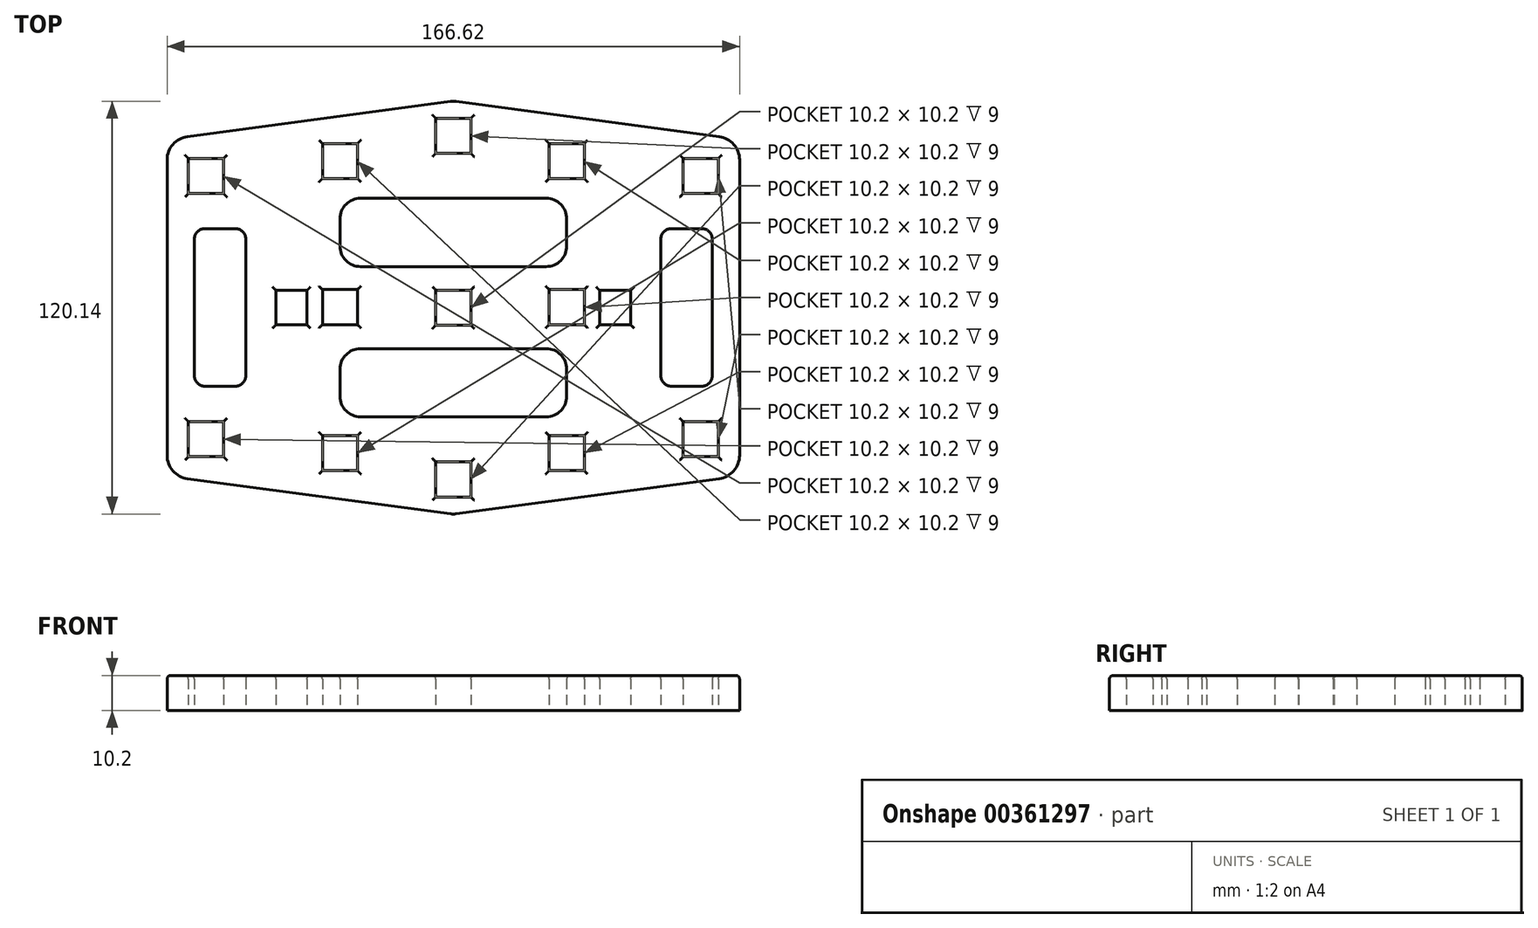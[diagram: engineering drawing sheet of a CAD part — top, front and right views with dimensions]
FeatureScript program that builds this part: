
annotation { "Feature Type Name" : "Feature", "Feature Type Description" : "" }
export const myFeature = defineFeature(function(context is Context, id is Id, definition is map)
    precondition{}
    {
        {
            var Q0;
            Q0=qCreatedBy(makeId("Top.planeOp"),FACE);
            var sketch = newSketch(context, id + "F0", { "sketchPlane" : qUnion([Q0])});
            skLineSegment(sketch, "E0.bottom", {"start": v(5.1, -5.1) * mm, "end": v(-5.1, -5.1) * mm});
            skLineSegment(sketch, "E0.top", {"start": v(5.1, 5.1) * mm, "end": v(-5.1, 5.1) * mm});
            skLineSegment(sketch, "E0.left", {"start": v(5.1, -5.1) * mm, "end": v(5.1, 5.1) * mm});
            skLineSegment(sketch, "E0.right", {"start": v(-5.1, -5.1) * mm, "end": v(-5.1, 5.1) * mm});
            skPoint(sketch, "E0.middle", {"position": v(0, 0) * mm});
            skCircle(sketch, "E1", {"center": v(0, 0) * mm, "radius": 50 * mm, "construction": true});
            skLineSegment(sketch, "E2.bottom", {"start": v(5.1, 44.9) * mm, "end": v(-5.1, 44.9) * mm});
            skLineSegment(sketch, "E2.top", {"start": v(5.1, 55.1) * mm, "end": v(-5.1, 55.1) * mm});
            skLineSegment(sketch, "E2.left", {"start": v(5.1, 44.9) * mm, "end": v(5.1, 55.1) * mm});
            skLineSegment(sketch, "E2.right", {"start": v(-5.1, 44.9) * mm, "end": v(-5.1, 55.1) * mm});
            skPoint(sketch, "E2.middle", {"position": v(0, 50) * mm});
            skLineSegment(sketch, "E3.bottom", {"start": v(5.1, -55.1) * mm, "end": v(-5.1, -55.1) * mm});
            skLineSegment(sketch, "E3.top", {"start": v(5.1, -44.9) * mm, "end": v(-5.1, -44.9) * mm});
            skLineSegment(sketch, "E3.left", {"start": v(5.1, -55.1) * mm, "end": v(5.1, -44.9) * mm});
            skLineSegment(sketch, "E3.right", {"start": v(-5.1, -55.1) * mm, "end": v(-5.1, -44.9) * mm});
            skPoint(sketch, "E3.middle", {"position": v(0, -50) * mm});
            skCircle(sketch, "E4", {"center": v(0, 0) * mm, "radius": 33 * mm, "construction": true});
            skLineSegment(sketch, "E5", {"start": v(-33, 25.81) * mm, "end": v(-33, 17.94) * mm});
            skCircle(sketch, "E6", {"center": v(-33, 0.15) * mm, "radius": 42.5 * mm, "construction": true});
            skPoint(sketch, "E7.middle", {"position": v(-33, 42.65) * mm});
            skLineSegment(sketch, "E8.bottom", {"start": v(-27.9, 5.25) * mm, "end": v(-38.1, 5.25) * mm});
            skLineSegment(sketch, "E8.top", {"start": v(-27.9, -4.95) * mm, "end": v(-38.1, -4.95) * mm});
            skLineSegment(sketch, "E8.left", {"start": v(-27.9, 5.25) * mm, "end": v(-27.9, -4.95) * mm});
            skLineSegment(sketch, "E8.right", {"start": v(-38.1, 5.25) * mm, "end": v(-38.1, -4.95) * mm});
            skLineSegment(sketch, "E9.bottom", {"start": v(-38.1, 37.55) * mm, "end": v(-27.9, 37.55) * mm});
            skLineSegment(sketch, "E9.top", {"start": v(-38.1, 47.75) * mm, "end": v(-27.9, 47.75) * mm});
            skLineSegment(sketch, "E9.left", {"start": v(-38.1, 37.55) * mm, "end": v(-38.1, 47.75) * mm});
            skLineSegment(sketch, "E9.right", {"start": v(-27.9, 37.55) * mm, "end": v(-27.9, 47.75) * mm});
            skLineSegment(sketch, "E10.bottom", {"start": v(-27.9, -47.45) * mm, "end": v(-38.1, -47.45) * mm});
            skLineSegment(sketch, "E10.top", {"start": v(-27.9, -37.25) * mm, "end": v(-38.1, -37.25) * mm});
            skLineSegment(sketch, "E10.left", {"start": v(-27.9, -47.45) * mm, "end": v(-27.9, -37.25) * mm});
            skLineSegment(sketch, "E10.right", {"start": v(-38.1, -47.45) * mm, "end": v(-38.1, -37.25) * mm});
            skPoint(sketch, "E10.middle", {"position": v(-33, -42.35) * mm});
            skCircle(sketch, "E11", {"center": v(-33, 0.15) * mm, "radius": 39 * mm, "construction": true});
            skLineSegment(sketch, "E12", {"start": v(-72, 50.1) * mm, "end": v(-72, -61.27) * mm, "construction": true});
            skCircle(sketch, "E13", {"center": v(-72, 0) * mm, "radius": 38.3 * mm, "construction": true});
            skLineSegment(sketch, "E14.bottom", {"start": v(-77.1, 33.2) * mm, "end": v(-66.9, 33.2) * mm});
            skLineSegment(sketch, "E14.top", {"start": v(-77.1, 43.4) * mm, "end": v(-66.9, 43.4) * mm});
            skLineSegment(sketch, "E14.left", {"start": v(-77.1, 33.2) * mm, "end": v(-77.1, 43.4) * mm});
            skLineSegment(sketch, "E14.right", {"start": v(-66.9, 33.2) * mm, "end": v(-66.9, 43.4) * mm});
            skPoint(sketch, "E14.middle", {"position": v(-72, 38.3) * mm});
            skLineSegment(sketch, "E15.bottom", {"start": v(-77.1, -43.4) * mm, "end": v(-66.9, -43.4) * mm});
            skLineSegment(sketch, "E15.top", {"start": v(-77.1, -33.2) * mm, "end": v(-66.9, -33.2) * mm});
            skLineSegment(sketch, "E15.left", {"start": v(-77.1, -43.4) * mm, "end": v(-77.1, -33.2) * mm});
            skLineSegment(sketch, "E15.right", {"start": v(-66.9, -43.4) * mm, "end": v(-66.9, -33.2) * mm});
            skPoint(sketch, "E15.middle", {"position": v(-72, -38.3) * mm});
            skLineSegment(sketch, "E16.MirrorCS", {"start": v(27.9, -4.95) * mm, "end": v(38.1, -4.95) * mm});
            skPoint(sketch, "E17.MirrorP", {"position": v(33, 42.65) * mm});
            skLineSegment(sketch, "E18.MirrorCS", {"start": v(66.9, 33.2) * mm, "end": v(66.9, 43.4) * mm});
            skLineSegment(sketch, "E19.MirrorCS", {"start": v(27.9, 5.25) * mm, "end": v(27.9, -4.95) * mm});
            skLineSegment(sketch, "E20.MirrorCS", {"start": v(66.9, -43.4) * mm, "end": v(66.9, -33.2) * mm});
            skLineSegment(sketch, "E21.MirrorCS", {"start": v(77.1, 33.2) * mm, "end": v(66.9, 33.2) * mm});
            skLineSegment(sketch, "E22.MirrorCS", {"start": v(38.1, 37.55) * mm, "end": v(38.1, 47.75) * mm});
            skLineSegment(sketch, "E23.MirrorCS", {"start": v(27.9, -37.25) * mm, "end": v(38.1, -37.25) * mm});
            skLineSegment(sketch, "E24.MirrorCS", {"start": v(77.1, 33.2) * mm, "end": v(77.1, 43.4) * mm});
            skLineSegment(sketch, "E25.MirrorCS", {"start": v(77.1, -43.4) * mm, "end": v(77.1, -33.2) * mm});
            skLineSegment(sketch, "E26.MirrorCS", {"start": v(38.1, 5.25) * mm, "end": v(38.1, -4.95) * mm});
            skPoint(sketch, "E27.MirrorP", {"position": v(33, 0.15) * mm});
            skLineSegment(sketch, "E28.MirrorCS", {"start": v(38.1, 37.55) * mm, "end": v(27.9, 37.55) * mm});
            skLineSegment(sketch, "E29.MirrorCS", {"start": v(27.9, 37.55) * mm, "end": v(27.9, 47.75) * mm});
            skPoint(sketch, "E30.MirrorP", {"position": v(72, 38.3) * mm});
            skLineSegment(sketch, "E31.MirrorCS", {"start": v(38.1, -47.45) * mm, "end": v(38.1, -37.25) * mm});
            skLineSegment(sketch, "E32.MirrorCS", {"start": v(38.1, 47.75) * mm, "end": v(27.9, 47.75) * mm});
            skLineSegment(sketch, "E33.MirrorCS", {"start": v(77.1, -33.2) * mm, "end": v(66.9, -33.2) * mm});
            skLineSegment(sketch, "E34.MirrorCS", {"start": v(33, 25.81) * mm, "end": v(33, 17.94) * mm});
            skLineSegment(sketch, "E35.MirrorCS", {"start": v(72, 50.1) * mm, "end": v(72, -61.27) * mm, "construction": true});
            skLineSegment(sketch, "E36.MirrorCS", {"start": v(27.9, 5.25) * mm, "end": v(38.1, 5.25) * mm});
            skLineSegment(sketch, "E37.MirrorCS", {"start": v(77.1, -43.4) * mm, "end": v(66.9, -43.4) * mm});
            skLineSegment(sketch, "E38.MirrorCS", {"start": v(77.1, 43.4) * mm, "end": v(66.9, 43.4) * mm});
            skPoint(sketch, "E39.MirrorP", {"position": v(72, -38.3) * mm});
            skLineSegment(sketch, "E40.MirrorCS", {"start": v(27.9, -47.45) * mm, "end": v(27.9, -37.25) * mm});
            skLineSegment(sketch, "E41.MirrorCS", {"start": v(27.9, -47.45) * mm, "end": v(38.1, -47.45) * mm});
            skPoint(sketch, "E42.MirrorP", {"position": v(33, -42.35) * mm});
            skLineSegment(sketch, "E43", {"start": v(-0.8, 60.02) * mm, "end": v(-52.3, 53.14) * mm});
            skLineSegment(sketch, "E44", {"start": v(-83.3, 43) * mm, "end": v(-83.3, 0) * mm});
            skPoint(sketch, "E45.visualSharp", {"position": v(-83.3, 49) * mm});
            skLineSegment(sketch, "E46.MirrorCS", {"start": v(-0.8, -60.02) * mm, "end": v(-52.3, -53.14) * mm});
            skLineSegment(sketch, "E47.MirrorCS", {"start": v(-83.3, -43) * mm, "end": v(-83.3, 0) * mm});
            skLineSegment(sketch, "E48.MirrorCS", {"start": v(0.8, -60.02) * mm, "end": v(52.3, -53.14) * mm});
            skLineSegment(sketch, "E49.MirrorCS", {"start": v(83.3, -43) * mm, "end": v(83.3, 0) * mm});
            skLineSegment(sketch, "E50.MirrorCS", {"start": v(0.8, 60.02) * mm, "end": v(52.3, 53.14) * mm});
            skLineSegment(sketch, "E51.MirrorCS", {"start": v(83.3, 43) * mm, "end": v(83.3, 0) * mm});
            skPoint(sketch, "E52.visualSharp", {"position": v(0, 60.12) * mm});
            skArc(sketch, "E52.filletArc", {"start": v(0.8, 60.02) * mm, "mid": v(0, 60.07) * mm, "end": v(-0.8, 60.02) * mm});
            skPoint(sketch, "E53.visualSharp", {"position": v(0, -60.12) * mm});
            skArc(sketch, "E53.filletArc", {"start": v(-0.8, -60.02) * mm, "mid": v(0, -60.07) * mm, "end": v(0.8, -60.02) * mm});
            skPoint(sketch, "E54.visualSharp", {"position": v(-75.36, 23) * mm});
            skPoint(sketch, "E55.visualSharp", {"position": v(-44.4, 23) * mm});
            skPoint(sketch, "E56.visualSharp", {"position": v(-44.4, -22.92) * mm});
            skPoint(sketch, "E57.visualSharp", {"position": v(-75.36, -22.92) * mm});
            skLineSegment(sketch, "E58.bottom", {"start": v(-27, 31.81) * mm, "end": v(27, 31.81) * mm});
            skLineSegment(sketch, "E58.top", {"start": v(-27, 11.94) * mm, "end": v(27, 11.94) * mm});
            skPoint(sketch, "E59.newPointB", {"position": v(-33, 73.57) * mm});
            skArc(sketch, "E59.filletArc", {"start": v(-27, 31.81) * mm, "mid": v(-31.24, 30.05) * mm, "end": v(-33, 25.81) * mm});
            skPoint(sketch, "E60.newPointA", {"position": v(-33, -73.26) * mm});
            skArc(sketch, "E60.filletArc", {"start": v(-33, 17.94) * mm, "mid": v(-31.24, 13.7) * mm, "end": v(-27, 11.94) * mm});
            skPoint(sketch, "E61.newPointB", {"position": v(33, -73.26) * mm});
            skArc(sketch, "E61.filletArc", {"start": v(27, 11.94) * mm, "mid": v(31.24, 13.7) * mm, "end": v(33, 17.94) * mm});
            skPoint(sketch, "E62.newPointB", {"position": v(33, 73.57) * mm});
            skArc(sketch, "E62.filletArc", {"start": v(33, 25.81) * mm, "mid": v(31.24, 30.05) * mm, "end": v(27, 31.81) * mm});
            skLineSegment(sketch, "E63.MirrorCS", {"start": v(-27, -31.81) * mm, "end": v(27, -31.81) * mm});
            skArc(sketch, "E64.MirrorCS", {"start": v(33, -25.81) * mm, "mid": v(31.24, -30.05) * mm, "end": v(27, -31.81) * mm});
            skLineSegment(sketch, "E65.MirrorCS", {"start": v(-33, -25.81) * mm, "end": v(-33, -17.94) * mm});
            skLineSegment(sketch, "E66.MirrorCS", {"start": v(33, -25.81) * mm, "end": v(33, -17.94) * mm});
            skArc(sketch, "E67.MirrorCS", {"start": v(27, -11.94) * mm, "mid": v(31.24, -13.7) * mm, "end": v(33, -17.94) * mm});
            skLineSegment(sketch, "E68.MirrorCS", {"start": v(-27, -11.94) * mm, "end": v(27, -11.94) * mm});
            skArc(sketch, "E69.MirrorCS", {"start": v(-33, -17.94) * mm, "mid": v(-31.24, -13.7) * mm, "end": v(-27, -11.94) * mm});
            skArc(sketch, "E70.MirrorCS", {"start": v(-27, -31.81) * mm, "mid": v(-31.24, -30.05) * mm, "end": v(-33, -25.81) * mm});
            skCircle(sketch, "E71", {"center": v(-42.1, 0) * mm, "radius": 5 * mm, "construction": true});
            skLineSegment(sketch, "E72.bottom", {"start": v(-51.6, -5) * mm, "end": v(-42.6, -5) * mm});
            skLineSegment(sketch, "E72.top", {"start": v(-51.6, 5) * mm, "end": v(-42.6, 5) * mm});
            skLineSegment(sketch, "E72.left", {"start": v(-51.6, -5) * mm, "end": v(-51.6, 5) * mm});
            skLineSegment(sketch, "E72.right", {"start": v(-42.6, -5) * mm, "end": v(-42.6, 5) * mm});
            skPoint(sketch, "E72.middle", {"position": v(-47.1, 0) * mm});
            skLineSegment(sketch, "E73.MirrorCS", {"start": v(51.6, -5) * mm, "end": v(51.6, 5) * mm});
            skLineSegment(sketch, "E74.MirrorCS", {"start": v(51.6, -5) * mm, "end": v(42.6, -5) * mm});
            skLineSegment(sketch, "E75.MirrorCS", {"start": v(51.6, 5) * mm, "end": v(42.6, 5) * mm});
            skLineSegment(sketch, "E76.MirrorCS", {"start": v(42.6, -5) * mm, "end": v(42.6, 5) * mm});
            skLineSegment(sketch, "E77.bottom", {"start": v(-72.36, 23) * mm, "end": v(-63.43, 23) * mm});
            skLineSegment(sketch, "E77.top", {"start": v(-72.36, -22.88) * mm, "end": v(-63.43, -22.88) * mm});
            skLineSegment(sketch, "E77.left", {"start": v(-75.36, 20) * mm, "end": v(-75.36, -19.88) * mm});
            skLineSegment(sketch, "E77.right", {"start": v(-60.43, 20) * mm, "end": v(-60.43, -19.88) * mm});
            skArc(sketch, "E78.filletArc", {"start": v(-72.36, 23) * mm, "mid": v(-74.48, 22.12) * mm, "end": v(-75.36, 20) * mm});
            skPoint(sketch, "E79.visualSharp", {"position": v(-75.36, -22.88) * mm});
            skArc(sketch, "E79.filletArc", {"start": v(-75.36, -19.88) * mm, "mid": v(-74.48, -22) * mm, "end": v(-72.36, -22.88) * mm});
            skPoint(sketch, "E80.visualSharp", {"position": v(-60.43, 23) * mm});
            skArc(sketch, "E80.filletArc", {"start": v(-60.43, 20) * mm, "mid": v(-61.3, 22.12) * mm, "end": v(-63.43, 23) * mm});
            skPoint(sketch, "E81.visualSharp", {"position": v(-60.43, -22.88) * mm});
            skArc(sketch, "E81.filletArc", {"start": v(-63.43, -22.88) * mm, "mid": v(-61.3, -22) * mm, "end": v(-60.43, -19.88) * mm});
            skArc(sketch, "E82.MirrorCS", {"start": v(60.43, 20) * mm, "mid": v(61.3, 22.12) * mm, "end": v(63.43, 23) * mm});
            skLineSegment(sketch, "E83.MirrorCS", {"start": v(60.43, 20) * mm, "end": v(60.43, -19.88) * mm});
            skArc(sketch, "E84.MirrorCS", {"start": v(63.43, -22.88) * mm, "mid": v(61.3, -22) * mm, "end": v(60.43, -19.88) * mm});
            skLineSegment(sketch, "E85.MirrorCS", {"start": v(72.36, -22.88) * mm, "end": v(63.43, -22.88) * mm});
            skArc(sketch, "E86.MirrorCS", {"start": v(75.36, -19.88) * mm, "mid": v(74.48, -22) * mm, "end": v(72.36, -22.88) * mm});
            skLineSegment(sketch, "E87.MirrorCS", {"start": v(72.36, 23) * mm, "end": v(63.43, 23) * mm});
            skLineSegment(sketch, "E88.MirrorCS", {"start": v(75.36, 20) * mm, "end": v(75.36, -19.88) * mm});
            skArc(sketch, "E89.MirrorCS", {"start": v(72.36, 23) * mm, "mid": v(74.48, 22.12) * mm, "end": v(75.36, 20) * mm});
            skLineSegment(sketch, "E90.trimOffspring", {"start": v(-62.22, 51.81) * mm, "end": v(-77.36, 49.8) * mm});
            skLineSegment(sketch, "E91.trimOffspring", {"start": v(62.22, 51.81) * mm, "end": v(77.36, 49.8) * mm});
            skLineSegment(sketch, "E92.trimOffspring", {"start": v(-62.22, -51.81) * mm, "end": v(-77.36, -49.8) * mm});
            skLineSegment(sketch, "E93.trimOffspring", {"start": v(62.22, -51.81) * mm, "end": v(77.36, -49.8) * mm});
            skLineSegment(sketch, "E94", {"start": v(-62.22, 51.81) * mm, "end": v(-52.3, 53.14) * mm});
            skLineSegment(sketch, "E95", {"start": v(52.3, 53.14) * mm, "end": v(62.22, 51.81) * mm});
            skLineSegment(sketch, "E96", {"start": v(62.22, -51.81) * mm, "end": v(52.3, -53.14) * mm});
            skLineSegment(sketch, "E97", {"start": v(-52.3, -53.14) * mm, "end": v(-62.22, -51.81) * mm});
            skPoint(sketch, "E98.orphan", {"position": v(-83.3, 43.74) * mm});
            skPoint(sketch, "E99.orphan", {"position": v(83.3, 43.74) * mm});
            skPoint(sketch, "E100.orphan", {"position": v(83.3, -43.74) * mm});
            skPoint(sketch, "E101.orphan", {"position": v(-83.3, -43.74) * mm});
            skPoint(sketch, "E102.newPointA", {"position": v(-78.1, 49.7) * mm});
            skArc(sketch, "E102.filletArc", {"start": v(-77.36, 49.8) * mm, "mid": v(-81.61, 47.51) * mm, "end": v(-83.3, 43) * mm});
            skArc(sketch, "E103.MirrorCS", {"start": v(77.36, 49.8) * mm, "mid": v(81.61, 47.51) * mm, "end": v(83.3, 43) * mm});
            skPoint(sketch, "E104.orphan", {"position": v(78.1, 49.7) * mm});
            skArc(sketch, "E105.MirrorCS", {"start": v(-77.36, -49.8) * mm, "mid": v(-81.61, -47.51) * mm, "end": v(-83.3, -43) * mm});
            skPoint(sketch, "E106.orphan", {"position": v(-78.1, -49.7) * mm});
            skArc(sketch, "E107.MirrorCS", {"start": v(77.36, -49.8) * mm, "mid": v(81.61, -47.51) * mm, "end": v(83.3, -43) * mm});
            skPoint(sketch, "E108.orphan", {"position": v(78.1, -49.7) * mm});
            skSolve(sketch);
        }
        {
            var Q0;
            Q0=makeQuery(id+"F0.imprint","IMPRINT",FACE,{"disambiguationData":[TD([[makeQuery(id+"F0.imprint","IMPRINT",EDGE,{"derivedFrom":sQuery(id+"F0.wireOp",EDGE,"E0.bottom")}),1.0]])]});
            extrude(context, id + "F1", {"entities" : qUnion([Q0]), "depth" : 10 * mm});
        }
        {
            var Q0;
            Q0=makeQuery(id+"F1.opExtrude","CAP_FACE",FACE,{"disambiguationData":[OSD([sQuery(id+"F0.wireOp",EDGE,"E0.bottom"),sQuery(id+"F0.wireOp",EDGE,"E0.top"),sQuery(id+"F0.wireOp",EDGE,"E0.left"),sQuery(id+"F0.wireOp",EDGE,"E0.right"),sQuery(id+"F0.wireOp",EDGE,"E2.bottom"),sQuery(id+"F0.wireOp",EDGE,"E2.top"),sQuery(id+"F0.wireOp",EDGE,"E2.left"),sQuery(id+"F0.wireOp",EDGE,"E2.right"),sQuery(id+"F0.wireOp",EDGE,"E3.bottom"),sQuery(id+"F0.wireOp",EDGE,"E3.top"),sQuery(id+"F0.wireOp",EDGE,"E3.left"),sQuery(id+"F0.wireOp",EDGE,"E3.right"),sQuery(id+"F0.wireOp",EDGE,"E8.bottom"),sQuery(id+"F0.wireOp",EDGE,"E8.top"),sQuery(id+"F0.wireOp",EDGE,"E8.left"),sQuery(id+"F0.wireOp",EDGE,"E8.right"),sQuery(id+"F0.wireOp",EDGE,"E9.bottom"),sQuery(id+"F0.wireOp",EDGE,"E9.top"),sQuery(id+"F0.wireOp",EDGE,"E9.left"),sQuery(id+"F0.wireOp",EDGE,"E9.right"),sQuery(id+"F0.wireOp",EDGE,"E10.bottom"),sQuery(id+"F0.wireOp",EDGE,"E10.top"),sQuery(id+"F0.wireOp",EDGE,"E10.left"),sQuery(id+"F0.wireOp",EDGE,"E10.right"),sQuery(id+"F0.wireOp",EDGE,"E14.bottom"),sQuery(id+"F0.wireOp",EDGE,"E14.top"),sQuery(id+"F0.wireOp",EDGE,"E14.left"),sQuery(id+"F0.wireOp",EDGE,"E14.right"),sQuery(id+"F0.wireOp",EDGE,"E15.bottom"),sQuery(id+"F0.wireOp",EDGE,"E15.top"),sQuery(id+"F0.wireOp",EDGE,"E15.left"),sQuery(id+"F0.wireOp",EDGE,"E15.right"),sQuery(id+"F0.wireOp",EDGE,"E16.MirrorCS"),sQuery(id+"F0.wireOp",EDGE,"E18.MirrorCS"),sQuery(id+"F0.wireOp",EDGE,"E19.MirrorCS"),sQuery(id+"F0.wireOp",EDGE,"E20.MirrorCS"),sQuery(id+"F0.wireOp",EDGE,"E21.MirrorCS"),sQuery(id+"F0.wireOp",EDGE,"E22.MirrorCS"),sQuery(id+"F0.wireOp",EDGE,"E23.MirrorCS"),sQuery(id+"F0.wireOp",EDGE,"E24.MirrorCS"),sQuery(id+"F0.wireOp",EDGE,"E25.MirrorCS"),sQuery(id+"F0.wireOp",EDGE,"E26.MirrorCS"),sQuery(id+"F0.wireOp",EDGE,"E28.MirrorCS"),sQuery(id+"F0.wireOp",EDGE,"E29.MirrorCS"),sQuery(id+"F0.wireOp",EDGE,"E31.MirrorCS"),sQuery(id+"F0.wireOp",EDGE,"E32.MirrorCS"),sQuery(id+"F0.wireOp",EDGE,"E33.MirrorCS"),sQuery(id+"F0.wireOp",EDGE,"E36.MirrorCS"),sQuery(id+"F0.wireOp",EDGE,"E37.MirrorCS"),sQuery(id+"F0.wireOp",EDGE,"E38.MirrorCS"),sQuery(id+"F0.wireOp",EDGE,"E40.MirrorCS"),sQuery(id+"F0.wireOp",EDGE,"E41.MirrorCS"),sQuery(id+"F0.wireOp",EDGE,"E43"),sQuery(id+"F0.wireOp",EDGE,"E44"),sQuery(id+"F0.wireOp",EDGE,"E47.MirrorCS"),sQuery(id+"F0.wireOp",EDGE,"E46.MirrorCS"),sQuery(id+"F0.wireOp",EDGE,"E48.MirrorCS"),sQuery(id+"F0.wireOp",EDGE,"E49.MirrorCS"),sQuery(id+"F0.wireOp",EDGE,"E50.MirrorCS"),sQuery(id+"F0.wireOp",EDGE,"E51.MirrorCS"),sQuery(id+"F0.wireOp",EDGE,"E52.filletArc"),sQuery(id+"F0.wireOp",EDGE,"E53.filletArc"),sQuery(id+"F0.wireOp",EDGE,"E58.bottom"),sQuery(id+"F0.wireOp",EDGE,"E58.top"),sQuery(id+"F0.wireOp",EDGE,"E5"),sQuery(id+"F0.wireOp",EDGE,"E34.MirrorCS"),sQuery(id+"F0.wireOp",EDGE,"E59.filletArc"),sQuery(id+"F0.wireOp",EDGE,"E60.filletArc"),sQuery(id+"F0.wireOp",EDGE,"E61.filletArc"),sQuery(id+"F0.wireOp",EDGE,"E62.filletArc"),sQuery(id+"F0.wireOp",EDGE,"E63.MirrorCS"),sQuery(id+"F0.wireOp",EDGE,"E64.MirrorCS"),sQuery(id+"F0.wireOp",EDGE,"E65.MirrorCS"),sQuery(id+"F0.wireOp",EDGE,"E66.MirrorCS"),sQuery(id+"F0.wireOp",EDGE,"E67.MirrorCS"),sQuery(id+"F0.wireOp",EDGE,"E68.MirrorCS"),sQuery(id+"F0.wireOp",EDGE,"E69.MirrorCS"),sQuery(id+"F0.wireOp",EDGE,"E70.MirrorCS"),sQuery(id+"F0.wireOp",EDGE,"E72.bottom"),sQuery(id+"F0.wireOp",EDGE,"E72.top"),sQuery(id+"F0.wireOp",EDGE,"E72.left"),sQuery(id+"F0.wireOp",EDGE,"E72.right"),sQuery(id+"F0.wireOp",EDGE,"E73.MirrorCS"),sQuery(id+"F0.wireOp",EDGE,"E74.MirrorCS"),sQuery(id+"F0.wireOp",EDGE,"E75.MirrorCS"),sQuery(id+"F0.wireOp",EDGE,"E76.MirrorCS"),sQuery(id+"F0.wireOp",EDGE,"E77.bottom"),sQuery(id+"F0.wireOp",EDGE,"E77.top"),sQuery(id+"F0.wireOp",EDGE,"E77.left"),sQuery(id+"F0.wireOp",EDGE,"E77.right"),sQuery(id+"F0.wireOp",EDGE,"E78.filletArc"),sQuery(id+"F0.wireOp",EDGE,"E79.filletArc"),sQuery(id+"F0.wireOp",EDGE,"E80.filletArc"),sQuery(id+"F0.wireOp",EDGE,"E81.filletArc"),sQuery(id+"F0.wireOp",EDGE,"E82.MirrorCS"),sQuery(id+"F0.wireOp",EDGE,"E83.MirrorCS"),sQuery(id+"F0.wireOp",EDGE,"E84.MirrorCS"),sQuery(id+"F0.wireOp",EDGE,"E85.MirrorCS"),sQuery(id+"F0.wireOp",EDGE,"E86.MirrorCS"),sQuery(id+"F0.wireOp",EDGE,"E87.MirrorCS"),sQuery(id+"F0.wireOp",EDGE,"E88.MirrorCS"),sQuery(id+"F0.wireOp",EDGE,"E89.MirrorCS"),sQuery(id+"F0.wireOp",EDGE,"E90.trimOffspring"),sQuery(id+"F0.wireOp",EDGE,"E91.trimOffspring"),sQuery(id+"F0.wireOp",EDGE,"E92.trimOffspring"),sQuery(id+"F0.wireOp",EDGE,"E93.trimOffspring"),sQuery(id+"F0.wireOp",EDGE,"E94"),sQuery(id+"F0.wireOp",EDGE,"E95"),sQuery(id+"F0.wireOp",EDGE,"E96"),sQuery(id+"F0.wireOp",EDGE,"E97"),sQuery(id+"F0.wireOp",EDGE,"E102.filletArc"),sQuery(id+"F0.wireOp",EDGE,"E103.MirrorCS"),sQuery(id+"F0.wireOp",EDGE,"E105.MirrorCS"),sQuery(id+"F0.wireOp",EDGE,"E107.MirrorCS")])],"isStart":false});
            fillet(context, id + "F2", {"entities" : qUnion([Q0]), "radius" : 1 * mm, "tangentPropagation" : true, "allowEdgeOverflow" : false});
        }
        {
            var Q0;
            Q0=makeQuery(id+"F0.imprint","IMPRINT",FACE,{"disambiguationData":[TD([[makeQuery(id+"F0.imprint","IMPRINT",EDGE,{"derivedFrom":sQuery(id+"F0.wireOp",EDGE,"E9.bottom")}),1.0]])]});
            var Q1;
            Q1=makeQuery(id+"F0.imprint","IMPRINT",FACE,{"disambiguationData":[TD([[makeQuery(id+"F0.imprint","IMPRINT",EDGE,{"derivedFrom":sQuery(id+"F0.wireOp",EDGE,"E14.bottom")}),1.0]])]});
            var Q2;
            Q2=makeQuery(id+"F0.imprint","IMPRINT",FACE,{"disambiguationData":[TD([[makeQuery(id+"F0.imprint","IMPRINT",EDGE,{"derivedFrom":sQuery(id+"F0.wireOp",EDGE,"E77.bottom")}),-1.0]])]});
            var Q3;
            Q3=makeQuery(id+"F0.imprint","IMPRINT",FACE,{"disambiguationData":[TD([[makeQuery(id+"F0.imprint","IMPRINT",EDGE,{"derivedFrom":sQuery(id+"F0.wireOp",EDGE,"E58.bottom")}),-1.0]])]});
            var Q4;
            Q4=makeQuery(id+"F0.imprint","IMPRINT",FACE,{"disambiguationData":[TD([[makeQuery(id+"F0.imprint","IMPRINT",EDGE,{"derivedFrom":sQuery(id+"F0.wireOp",EDGE,"E2.bottom")}),-1.0]])]});
            var Q5;
            Q5=makeQuery(id+"F0.imprint","IMPRINT",FACE,{"disambiguationData":[TD([[makeQuery(id+"F0.imprint","IMPRINT",EDGE,{"derivedFrom":sQuery(id+"F0.wireOp",EDGE,"E22.MirrorCS")}),1.0]])]});
            var Q6;
            Q6=makeQuery(id+"F0.imprint","IMPRINT",FACE,{"disambiguationData":[TD([[makeQuery(id+"F0.imprint","IMPRINT",EDGE,{"derivedFrom":sQuery(id+"F0.wireOp",EDGE,"E18.MirrorCS")}),-1.0]])]});
            var Q7;
            Q7=makeQuery(id+"F0.imprint","IMPRINT",FACE,{"disambiguationData":[TD([[makeQuery(id+"F0.imprint","IMPRINT",EDGE,{"derivedFrom":sQuery(id+"F0.wireOp",EDGE,"E82.MirrorCS")}),-1.0]])]});
            var Q8;
            Q8=makeQuery(id+"F0.imprint","IMPRINT",FACE,{"disambiguationData":[TD([[makeQuery(id+"F0.imprint","IMPRINT",EDGE,{"derivedFrom":sQuery(id+"F0.wireOp",EDGE,"E73.MirrorCS")}),1.0]])]});
            var Q9;
            Q9=makeQuery(id+"F0.imprint","IMPRINT",FACE,{"disambiguationData":[TD([[makeQuery(id+"F0.imprint","IMPRINT",EDGE,{"derivedFrom":sQuery(id+"F0.wireOp",EDGE,"E16.MirrorCS")}),1.0]])]});
            var Q10;
            Q10=makeQuery(id+"F0.imprint","IMPRINT",FACE,{"disambiguationData":[TD([[makeQuery(id+"F0.imprint","IMPRINT",EDGE,{"derivedFrom":sQuery(id+"F0.wireOp",EDGE,"E0.bottom")}),-1.0]])]});
            var Q11;
            Q11=makeQuery(id+"F0.imprint","IMPRINT",FACE,{"disambiguationData":[TD([[makeQuery(id+"F0.imprint","IMPRINT",EDGE,{"derivedFrom":sQuery(id+"F0.wireOp",EDGE,"E63.MirrorCS")}),1.0]])]});
            var Q12;
            Q12=makeQuery(id+"F0.imprint","IMPRINT",FACE,{"disambiguationData":[TD([[makeQuery(id+"F0.imprint","IMPRINT",EDGE,{"derivedFrom":sQuery(id+"F0.wireOp",EDGE,"E8.bottom")}),1.0]])]});
            var Q13;
            Q13=makeQuery(id+"F0.imprint","IMPRINT",FACE,{"disambiguationData":[TD([[makeQuery(id+"F0.imprint","IMPRINT",EDGE,{"derivedFrom":sQuery(id+"F0.wireOp",EDGE,"E72.bottom")}),1.0]])]});
            var Q14;
            Q14=makeQuery(id+"F0.imprint","IMPRINT",FACE,{"disambiguationData":[TD([[makeQuery(id+"F0.imprint","IMPRINT",EDGE,{"derivedFrom":sQuery(id+"F0.wireOp",EDGE,"E15.bottom")}),1.0]])]});
            var Q15;
            Q15=makeQuery(id+"F0.imprint","IMPRINT",FACE,{"disambiguationData":[TD([[makeQuery(id+"F0.imprint","IMPRINT",EDGE,{"derivedFrom":sQuery(id+"F0.wireOp",EDGE,"E10.bottom")}),-1.0]])]});
            var Q16;
            Q16=makeQuery(id+"F0.imprint","IMPRINT",FACE,{"disambiguationData":[TD([[makeQuery(id+"F0.imprint","IMPRINT",EDGE,{"derivedFrom":sQuery(id+"F0.wireOp",EDGE,"E3.bottom")}),-1.0]])]});
            var Q17;
            Q17=makeQuery(id+"F0.imprint","IMPRINT",FACE,{"disambiguationData":[TD([[makeQuery(id+"F0.imprint","IMPRINT",EDGE,{"derivedFrom":sQuery(id+"F0.wireOp",EDGE,"E23.MirrorCS")}),-1.0]])]});
            var Q18;
            Q18=makeQuery(id+"F0.imprint","IMPRINT",FACE,{"disambiguationData":[TD([[makeQuery(id+"F0.imprint","IMPRINT",EDGE,{"derivedFrom":sQuery(id+"F0.wireOp",EDGE,"E20.MirrorCS")}),-1.0]])]});
            var Q19;
            Q19=makeQuery(id+"F0.imprint","IMPRINT",FACE,{"disambiguationData":[TD([[makeQuery(id+"F0.imprint","IMPRINT",EDGE,{"derivedFrom":sQuery(id+"F0.wireOp",EDGE,"E0.bottom")}),1.0]])]});
            extrude(context, id + "F3", {"entities" : qUnion([Q0, Q1, Q2, Q3, Q4, Q5, Q6, Q7, Q8, Q9, Q10, Q11, Q12, Q13, Q14, Q15, Q16, Q17, Q18, Q19]), "operationType" : NewBodyOperationType.ADD, "oppositeDirection" : true, "depth" : 0.2 * mm});
        }
    });
